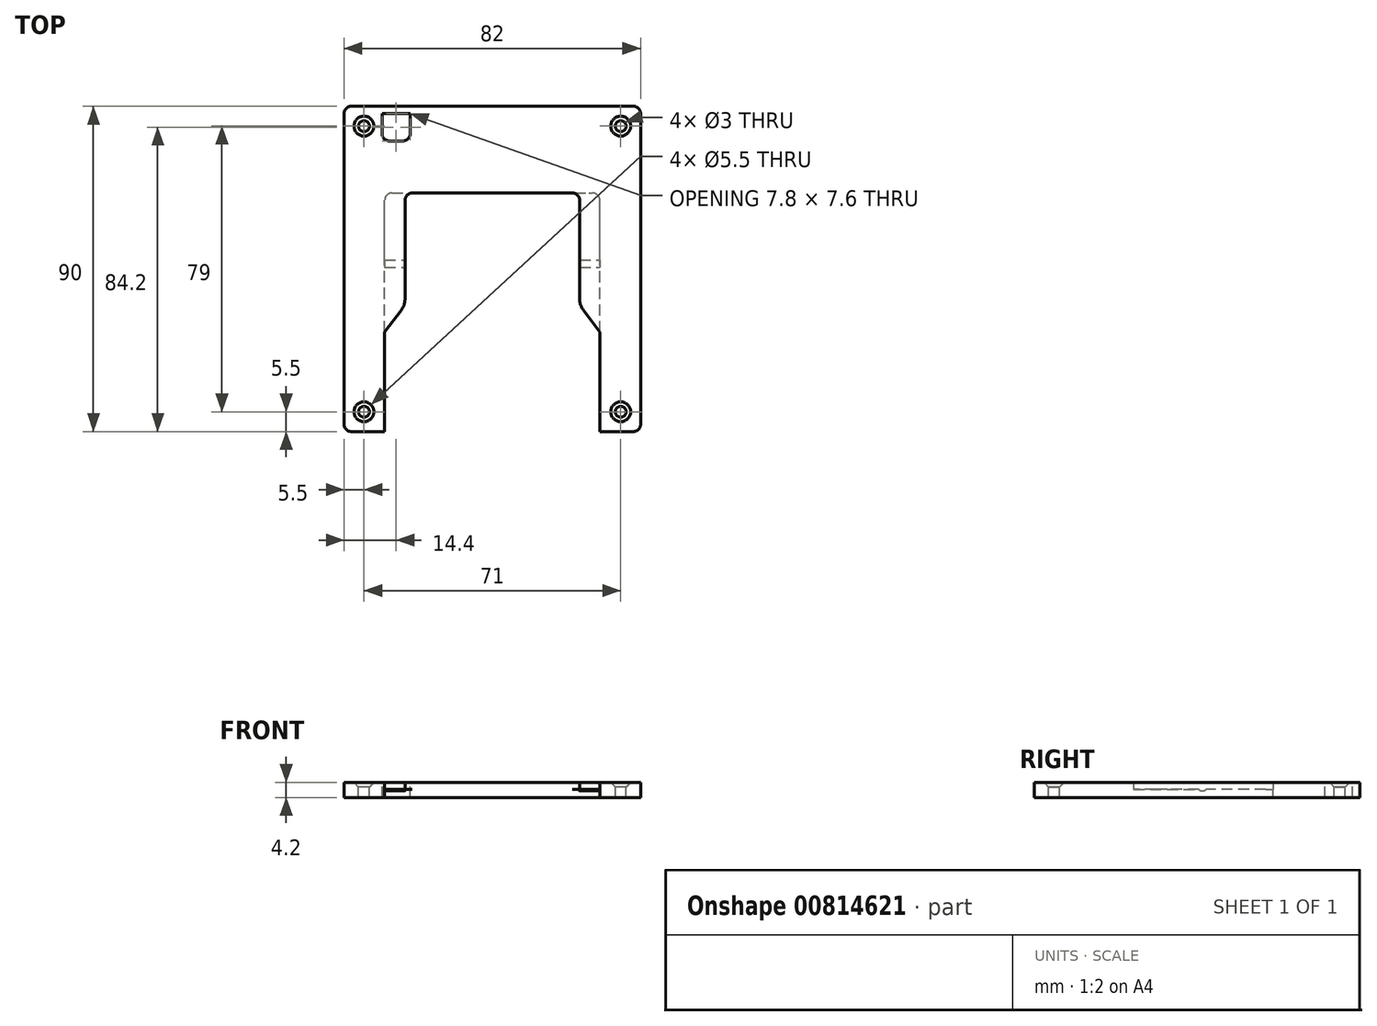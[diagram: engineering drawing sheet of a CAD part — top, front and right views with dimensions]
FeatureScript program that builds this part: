
annotation { "Feature Type Name" : "Feature", "Feature Type Description" : "" }
export const myFeature = defineFeature(function(context is Context, id is Id, definition is map)
    precondition{}
    {
        {
            var Q0;
            Q0=qCreatedBy(makeId("Top.planeOp"),FACE);
            var sketch = newSketch(context, id + "F0", { "sketchPlane" : qUnion([Q0])});
            skLineSegment(sketch, "E0.bottom", {"start": v(2, 0) * mm, "end": v(80, 0) * mm});
            skLineSegment(sketch, "E0.top", {"start": v(2, -90) * mm, "end": v(11.25, -90) * mm});
            skLineSegment(sketch, "E0.left", {"start": v(0, -2) * mm, "end": v(0, -88) * mm});
            skLineSegment(sketch, "E0.right", {"start": v(82, -2) * mm, "end": v(82, -88) * mm});
            skPoint(sketch, "E1.visualSharp", {"position": v(0, 0) * mm});
            skArc(sketch, "E1.filletArc", {"start": v(2, 0) * mm, "mid": v(0.59, -0.59) * mm, "end": v(0, -2) * mm});
            skPoint(sketch, "E2.visualSharp", {"position": v(82, 0) * mm});
            skArc(sketch, "E2.filletArc", {"start": v(82, -2) * mm, "mid": v(81.41, -0.59) * mm, "end": v(80, 0) * mm});
            skPoint(sketch, "E3.visualSharp", {"position": v(82, -90) * mm});
            skArc(sketch, "E3.filletArc", {"start": v(80, -90) * mm, "mid": v(81.41, -89.41) * mm, "end": v(82, -88) * mm});
            skPoint(sketch, "E4.visualSharp", {"position": v(0, -90) * mm});
            skArc(sketch, "E4.filletArc", {"start": v(0, -88) * mm, "mid": v(0.59, -89.41) * mm, "end": v(2, -90) * mm});
            skLineSegment(sketch, "E5.top", {"start": v(18.85, -24) * mm, "end": v(63.15, -24) * mm});
            skLineSegment(sketch, "E5.left", {"start": v(11.25, -90) * mm, "end": v(11.25, -62.5) * mm});
            skLineSegment(sketch, "E5.right", {"start": v(70.75, -90) * mm, "end": v(70.75, -62.5) * mm});
            skLineSegment(sketch, "E6.trimOffspring", {"start": v(70.75, -90) * mm, "end": v(80, -90) * mm});
            skLineSegment(sketch, "E7.right", {"start": v(16.85, -26) * mm, "end": v(16.85, -53.34) * mm});
            skLineSegment(sketch, "E8.right", {"start": v(65.15, -26) * mm, "end": v(65.15, -53.34) * mm});
            skPoint(sketch, "E9.visualSharp", {"position": v(16.85, -24) * mm});
            skArc(sketch, "E9.filletArc", {"start": v(18.85, -24) * mm, "mid": v(17.44, -24.59) * mm, "end": v(16.85, -26) * mm});
            skPoint(sketch, "E10.visualSharp", {"position": v(65.15, -24) * mm});
            skArc(sketch, "E10.filletArc", {"start": v(65.15, -26) * mm, "mid": v(64.56, -24.59) * mm, "end": v(63.15, -24) * mm});
            skPoint(sketch, "E11", {"position": v(16.85, -55) * mm});
            skLineSegment(sketch, "E12", {"start": v(11.25, -62.5) * mm, "end": v(15.86, -56.33) * mm});
            skLineSegment(sketch, "E13", {"start": v(66.14, -56.33) * mm, "end": v(70.75, -62.5) * mm});
            skArc(sketch, "E14.filletArc", {"start": v(15.86, -56.33) * mm, "mid": v(16.6, -54.92) * mm, "end": v(16.85, -53.34) * mm});
            skPoint(sketch, "E15.visualSharp", {"position": v(65.15, -55) * mm});
            skArc(sketch, "E15.filletArc", {"start": v(65.15, -53.34) * mm, "mid": v(65.4, -54.92) * mm, "end": v(66.14, -56.33) * mm});
            skSolve(sketch);
        }
        {
            var Q0;
            Q0=makeQuery(id+"F0.imprint","IMPRINT",FACE,{"disambiguationData":[TD([[makeQuery(id+"F0.imprint","IMPRINT",EDGE,{"derivedFrom":sQuery(id+"F0.wireOp",EDGE,"E0.bottom")}),-1.0]])]});
            extrude(context, id + "F1", {"entities" : qUnion([Q0]), "depth" : 2 * mm, "offsetDistance" : 25 * mm});
        }
        {
            var Q0;
            Q0=makeQuery(id+"F1.opExtrude","CAP_FACE",FACE,{"disambiguationData":[OSD([sQuery(id+"F0.wireOp",EDGE,"E0.bottom"),sQuery(id+"F0.wireOp",EDGE,"E0.top"),sQuery(id+"F0.wireOp",EDGE,"E0.left"),sQuery(id+"F0.wireOp",EDGE,"E0.right"),sQuery(id+"F0.wireOp",EDGE,"E1.filletArc"),sQuery(id+"F0.wireOp",EDGE,"E2.filletArc"),sQuery(id+"F0.wireOp",EDGE,"E3.filletArc"),sQuery(id+"F0.wireOp",EDGE,"E4.filletArc"),sQuery(id+"F0.wireOp",EDGE,"E5.top"),sQuery(id+"F0.wireOp",EDGE,"E5.left"),sQuery(id+"F0.wireOp",EDGE,"E5.right"),sQuery(id+"F0.wireOp",EDGE,"E6.trimOffspring"),sQuery(id+"F0.wireOp",EDGE,"E7.right"),sQuery(id+"F0.wireOp",EDGE,"E8.right"),sQuery(id+"F0.wireOp",EDGE,"E9.filletArc"),sQuery(id+"F0.wireOp",EDGE,"E10.filletArc"),sQuery(id+"F0.wireOp",EDGE,"E12"),sQuery(id+"F0.wireOp",EDGE,"E13"),sQuery(id+"F0.wireOp",EDGE,"E14.filletArc"),sQuery(id+"F0.wireOp",EDGE,"E15.filletArc")])],"isStart":true});
            var sketch = newSketch(context, id + "F2", { "sketchPlane" : qUnion([Q0])});
            skArc(sketch, "E16.0", {"start": v(82, 2) * mm, "mid": v(81.41, 0.59) * mm, "end": v(80, 0) * mm});
            skLineSegment(sketch, "E16.1", {"start": v(2, 0) * mm, "end": v(80, 0) * mm});
            skArc(sketch, "E16.2", {"start": v(2, 0) * mm, "mid": v(0.59, 0.59) * mm, "end": v(0, 2) * mm});
            skLineSegment(sketch, "E16.3", {"start": v(0, 2) * mm, "end": v(0, 88) * mm});
            skArc(sketch, "E16.4", {"start": v(0, 88) * mm, "mid": v(0.59, 89.41) * mm, "end": v(2, 90) * mm});
            skLineSegment(sketch, "E16.5", {"start": v(82, 2) * mm, "end": v(82, 88) * mm});
            skLineSegment(sketch, "E16.6", {"start": v(2, 90) * mm, "end": v(11.25, 90) * mm});
            skLineSegment(sketch, "E16.7", {"start": v(11.25, 90) * mm, "end": v(11.25, 62.5) * mm});
            skLineSegment(sketch, "E16.9", {"start": v(70.75, 90) * mm, "end": v(70.75, 62.5) * mm});
            skLineSegment(sketch, "E16.10", {"start": v(70.75, 90) * mm, "end": v(80, 90) * mm});
            skArc(sketch, "E16.11", {"start": v(80, 90) * mm, "mid": v(81.41, 89.41) * mm, "end": v(82, 88) * mm});
            skLineSegment(sketch, "E16.14", {"start": v(16.85, 24) * mm, "end": v(65.15, 24) * mm});
            skLineSegment(sketch, "E17", {"start": v(70.75, 62.5) * mm, "end": v(70.75, 26) * mm});
            skLineSegment(sketch, "E18", {"start": v(68.75, 24) * mm, "end": v(65.15, 24) * mm});
            skPoint(sketch, "E19.visualSharp", {"position": v(70.75, 24) * mm});
            skArc(sketch, "E19.filletArc", {"start": v(68.75, 24) * mm, "mid": v(70.16, 24.59) * mm, "end": v(70.75, 26) * mm});
            skLineSegment(sketch, "E20", {"start": v(11.25, 62.5) * mm, "end": v(11.25, 26) * mm});
            skLineSegment(sketch, "E21", {"start": v(13.25, 24) * mm, "end": v(16.85, 24) * mm});
            skPoint(sketch, "E22.visualSharp", {"position": v(11.25, 24) * mm});
            skArc(sketch, "E22.filletArc", {"start": v(11.25, 26) * mm, "mid": v(11.84, 24.59) * mm, "end": v(13.25, 24) * mm});
            skSolve(sketch);
        }
        {
            var Q0;
            Q0=qSketchRegion(id+"F2",true);
            extrude(context, id + "F3", {"entities" : qUnion([Q0]), "operationType" : NewBodyOperationType.ADD, "depth" : 2.2 * mm, "offsetDistance" : 25 * mm});
        }
        {
            var Q0;
            Q0=makeQuery(id+"F1.opExtrude","CAP_FACE",FACE,{"disambiguationData":[OSD([sQuery(id+"F0.wireOp",EDGE,"E0.bottom"),sQuery(id+"F0.wireOp",EDGE,"E0.top"),sQuery(id+"F0.wireOp",EDGE,"E0.left"),sQuery(id+"F0.wireOp",EDGE,"E0.right"),sQuery(id+"F0.wireOp",EDGE,"E1.filletArc"),sQuery(id+"F0.wireOp",EDGE,"E2.filletArc"),sQuery(id+"F0.wireOp",EDGE,"E3.filletArc"),sQuery(id+"F0.wireOp",EDGE,"E4.filletArc"),sQuery(id+"F0.wireOp",EDGE,"E5.top"),sQuery(id+"F0.wireOp",EDGE,"E5.left"),sQuery(id+"F0.wireOp",EDGE,"E5.right"),sQuery(id+"F0.wireOp",EDGE,"E6.trimOffspring"),sQuery(id+"F0.wireOp",EDGE,"E7.right"),sQuery(id+"F0.wireOp",EDGE,"E8.right"),sQuery(id+"F0.wireOp",EDGE,"E9.filletArc"),sQuery(id+"F0.wireOp",EDGE,"E10.filletArc"),sQuery(id+"F0.wireOp",EDGE,"E12"),sQuery(id+"F0.wireOp",EDGE,"E13"),sQuery(id+"F0.wireOp",EDGE,"E14.filletArc"),sQuery(id+"F0.wireOp",EDGE,"E15.filletArc")])],"isStart":false});
            var sketch = newSketch(context, id + "F4", { "sketchPlane" : qUnion([Q0])});
            skLineSegment(sketch, "E23.bottom", {"start": v(10.5, -2) * mm, "end": v(18.3, -2) * mm});
            skLineSegment(sketch, "E23.top", {"start": v(12.5, -9.6) * mm, "end": v(16.3, -9.6) * mm});
            skLineSegment(sketch, "E23.left", {"start": v(10.5, -2) * mm, "end": v(10.5, -7.6) * mm});
            skLineSegment(sketch, "E23.right", {"start": v(18.3, -2) * mm, "end": v(18.3, -7.6) * mm});
            skPoint(sketch, "E24.visualSharp", {"position": v(10.5, -9.6) * mm});
            skArc(sketch, "E24.filletArc", {"start": v(10.5, -7.6) * mm, "mid": v(11.09, -9.01) * mm, "end": v(12.5, -9.6) * mm});
            skPoint(sketch, "E25.visualSharp", {"position": v(18.3, -9.6) * mm});
            skArc(sketch, "E25.filletArc", {"start": v(16.3, -9.6) * mm, "mid": v(17.71, -9.01) * mm, "end": v(18.3, -7.6) * mm});
            skSolve(sketch);
        }
        {
            var Q0;
            Q0=qSketchRegion(id+"F4",true);
            extrude(context, id + "F5", {"entities" : qUnion([Q0]), "operationType" : NewBodyOperationType.REMOVE, "oppositeDirection" : true, "depth" : 25 * mm, "offsetDistance" : 25 * mm});
        }
        {
            var Q0;
            Q0=makeQuery(id+"F1.opExtrude","CAP_FACE",FACE,{"disambiguationData":[OSD([sQuery(id+"F0.wireOp",EDGE,"E0.bottom"),sQuery(id+"F0.wireOp",EDGE,"E0.top"),sQuery(id+"F0.wireOp",EDGE,"E0.left"),sQuery(id+"F0.wireOp",EDGE,"E0.right"),sQuery(id+"F0.wireOp",EDGE,"E1.filletArc"),sQuery(id+"F0.wireOp",EDGE,"E2.filletArc"),sQuery(id+"F0.wireOp",EDGE,"E3.filletArc"),sQuery(id+"F0.wireOp",EDGE,"E4.filletArc"),sQuery(id+"F0.wireOp",EDGE,"E5.top"),sQuery(id+"F0.wireOp",EDGE,"E5.left"),sQuery(id+"F0.wireOp",EDGE,"E5.right"),sQuery(id+"F0.wireOp",EDGE,"E6.trimOffspring"),sQuery(id+"F0.wireOp",EDGE,"E7.right"),sQuery(id+"F0.wireOp",EDGE,"E8.right"),sQuery(id+"F0.wireOp",EDGE,"E9.filletArc"),sQuery(id+"F0.wireOp",EDGE,"E10.filletArc"),sQuery(id+"F0.wireOp",EDGE,"E12"),sQuery(id+"F0.wireOp",EDGE,"E13"),sQuery(id+"F0.wireOp",EDGE,"E14.filletArc"),sQuery(id+"F0.wireOp",EDGE,"E15.filletArc")])],"isStart":false});
            var sketch = newSketch(context, id + "F6", { "sketchPlane" : qUnion([Q0])});
            skCircle(sketch, "E26", {"center": v(5.5, -5.5) * mm, "radius": 1.5 * mm});
            skCircle(sketch, "E27", {"center": v(76.5, -5.5) * mm, "radius": 1.5 * mm});
            skCircle(sketch, "E28", {"center": v(5.5, -84.5) * mm, "radius": 1.5 * mm});
            skCircle(sketch, "E29", {"center": v(76.5, -84.5) * mm, "radius": 1.5 * mm});
            skSolve(sketch);
        }
        {
            var Q0;
            Q0=makeQuery(id+"F6.imprint","IMPRINT",FACE,{"disambiguationData":[TD([[makeQuery(id+"F6.imprint","IMPRINT",EDGE,{"derivedFrom":sQuery(id+"F6.wireOp",EDGE,"E28")}),1.0]])]});
            var Q1;
            Q1=makeQuery(id+"F6.imprint","IMPRINT",FACE,{"disambiguationData":[TD([[makeQuery(id+"F6.imprint","IMPRINT",EDGE,{"derivedFrom":sQuery(id+"F6.wireOp",EDGE,"E29")}),1.0]])]});
            var Q2;
            Q2=makeQuery(id+"F6.imprint","IMPRINT",FACE,{"disambiguationData":[TD([[makeQuery(id+"F6.imprint","IMPRINT",EDGE,{"derivedFrom":sQuery(id+"F6.wireOp",EDGE,"E26")}),1.0]])]});
            var Q3;
            Q3=makeQuery(id+"F6.imprint","IMPRINT",FACE,{"disambiguationData":[TD([[makeQuery(id+"F6.imprint","IMPRINT",EDGE,{"derivedFrom":sQuery(id+"F6.wireOp",EDGE,"E27")}),1.0]])]});
            extrude(context, id + "F7", {"entities" : qUnion([Q0, Q1, Q2, Q3]), "operationType" : NewBodyOperationType.REMOVE, "oppositeDirection" : true, "depth" : 4.2 * mm, "offsetDistance" : 25 * mm});
        }
        {
            var Q0;
            Q0=makeQuery(id+"F1.opExtrude","CAP_FACE",FACE,{"disambiguationData":[OSD([sQuery(id+"F0.wireOp",EDGE,"E0.bottom"),sQuery(id+"F0.wireOp",EDGE,"E0.top"),sQuery(id+"F0.wireOp",EDGE,"E0.left"),sQuery(id+"F0.wireOp",EDGE,"E0.right"),sQuery(id+"F0.wireOp",EDGE,"E1.filletArc"),sQuery(id+"F0.wireOp",EDGE,"E2.filletArc"),sQuery(id+"F0.wireOp",EDGE,"E3.filletArc"),sQuery(id+"F0.wireOp",EDGE,"E4.filletArc"),sQuery(id+"F0.wireOp",EDGE,"E5.top"),sQuery(id+"F0.wireOp",EDGE,"E5.left"),sQuery(id+"F0.wireOp",EDGE,"E5.right"),sQuery(id+"F0.wireOp",EDGE,"E6.trimOffspring"),sQuery(id+"F0.wireOp",EDGE,"E7.right"),sQuery(id+"F0.wireOp",EDGE,"E8.right"),sQuery(id+"F0.wireOp",EDGE,"E9.filletArc"),sQuery(id+"F0.wireOp",EDGE,"E10.filletArc"),sQuery(id+"F0.wireOp",EDGE,"E12"),sQuery(id+"F0.wireOp",EDGE,"E13"),sQuery(id+"F0.wireOp",EDGE,"E14.filletArc"),sQuery(id+"F0.wireOp",EDGE,"E15.filletArc")])],"isStart":false});
            var sketch = newSketch(context, id + "F8", { "sketchPlane" : qUnion([Q0])});
            skCircle(sketch, "E30", {"center": v(5.5, -5.5) * mm, "radius": 2.75 * mm});
            skCircle(sketch, "E31", {"center": v(76.5, -5.5) * mm, "radius": 2.75 * mm});
            skCircle(sketch, "E32", {"center": v(76.5, -84.5) * mm, "radius": 2.75 * mm});
            skCircle(sketch, "E33", {"center": v(5.5, -84.5) * mm, "radius": 2.75 * mm});
            skSolve(sketch);
        }
        {
            var Q0;
            Q0=qSketchRegion(id+"F8",true);
            extrude(context, id + "F9", {"entities" : qUnion([Q0]), "operationType" : NewBodyOperationType.REMOVE, "oppositeDirection" : true, "depth" : 1.6 * mm, "offsetDistance" : 25 * mm});
        }
        {
            var Q0;
            Q0=makeQuery(id+"F9.boolean.opBoolean","COPY",EDGE,{"derivedFrom":makeQuery(id+"F9.opExtrude","CAP_EDGE",EDGE,{"disambiguationData":[OSD([sQuery(id+"F8.wireOp",EDGE,"E33")])],"isStart":false})});
            var Q1;
            Q1=makeQuery(id+"F9.boolean.opBoolean","COPY",EDGE,{"derivedFrom":makeQuery(id+"F9.opExtrude","CAP_EDGE",EDGE,{"disambiguationData":[OSD([sQuery(id+"F8.wireOp",EDGE,"E32")])],"isStart":false})});
            var Q2;
            Q2=makeQuery(id+"F9.boolean.opBoolean","COPY",EDGE,{"derivedFrom":makeQuery(id+"F9.opExtrude","CAP_EDGE",EDGE,{"disambiguationData":[OSD([sQuery(id+"F8.wireOp",EDGE,"E30")])],"isStart":false})});
            var Q3;
            Q3=makeQuery(id+"F9.boolean.opBoolean","COPY",EDGE,{"derivedFrom":makeQuery(id+"F9.opExtrude","CAP_EDGE",EDGE,{"disambiguationData":[OSD([sQuery(id+"F8.wireOp",EDGE,"E31")])],"isStart":false})});
            chamfer(context, id + "F10", {"entities" : qUnion([Q0, Q1, Q2, Q3]), "width" : 1.5 * mm, "tangentPropagation" : true});
        }
        {
            var Q0;
            {var subQ0=sQuery(id+"F0.wireOp",EDGE,"E7.right");var subQ1=sQuery(id+"F0.wireOp",EDGE,"E9.filletArc");var subQ2=sQuery(id+"F0.wireOp",EDGE,"E5.left");var subQ3=sQuery(id+"F0.wireOp",EDGE,"E5.top");var subQ4=sQuery(id+"F0.wireOp",EDGE,"E12");var subQ5=sQuery(id+"F0.wireOp",EDGE,"E14.filletArc");Q0=makeQuery(id+"F3.boolean.opBoolean","SPLIT",FACE,{"disambiguationData":[TD([makeQuery(id+"F1.opExtrude","SWEPT_FACE",FACE,{"disambiguationData":[OSD([subQ2])]})])],"derivedFrom":makeQuery(id+"F1.opExtrude","CAP_FACE",FACE,{"disambiguationData":[OSD([sQuery(id+"F0.wireOp",EDGE,"E0.bottom"),sQuery(id+"F0.wireOp",EDGE,"E0.top"),sQuery(id+"F0.wireOp",EDGE,"E0.left"),sQuery(id+"F0.wireOp",EDGE,"E0.right"),sQuery(id+"F0.wireOp",EDGE,"E1.filletArc"),sQuery(id+"F0.wireOp",EDGE,"E2.filletArc"),sQuery(id+"F0.wireOp",EDGE,"E3.filletArc"),sQuery(id+"F0.wireOp",EDGE,"E4.filletArc"),subQ3,subQ2,sQuery(id+"F0.wireOp",EDGE,"E5.right"),sQuery(id+"F0.wireOp",EDGE,"E6.trimOffspring"),subQ0,sQuery(id+"F0.wireOp",EDGE,"E8.right"),subQ1,sQuery(id+"F0.wireOp",EDGE,"E10.filletArc"),subQ4,sQuery(id+"F0.wireOp",EDGE,"E13"),subQ5,sQuery(id+"F0.wireOp",EDGE,"E15.filletArc")])],"isStart":true})});}
            var sketch = newSketch(context, id + "F11", { "sketchPlane" : qUnion([Q0])});
            skLineSegment(sketch, "E34.bottom", {"start": v(11.25, 44.5) * mm, "end": v(16.85, 44.5) * mm});
            skLineSegment(sketch, "E34.top", {"start": v(11.25, 42.5) * mm, "end": v(16.85, 42.5) * mm});
            skLineSegment(sketch, "E34.left", {"start": v(11.25, 44.5) * mm, "end": v(11.25, 42.5) * mm});
            skLineSegment(sketch, "E34.right", {"start": v(16.85, 44.5) * mm, "end": v(16.85, 42.5) * mm});
            skLineSegment(sketch, "E35.bottom", {"start": v(65.15, 42.5) * mm, "end": v(70.75, 42.5) * mm});
            skLineSegment(sketch, "E35.top", {"start": v(65.15, 44.5) * mm, "end": v(70.75, 44.5) * mm});
            skLineSegment(sketch, "E35.left", {"start": v(65.15, 42.5) * mm, "end": v(65.15, 44.5) * mm});
            skLineSegment(sketch, "E35.right", {"start": v(70.75, 42.5) * mm, "end": v(70.75, 44.5) * mm});
            skSolve(sketch);
        }
        {
            var Q0;
            Q0=qSketchRegion(id+"F11",true);
            extrude(context, id + "F12", {"entities" : qUnion([Q0]), "operationType" : NewBodyOperationType.ADD, "depth" : 0.4 * mm, "offsetDistance" : 25 * mm});
        }
        {
            var Q0;
            Q0=makeQuery(id+"F12.opExtrude","CAP_EDGE",EDGE,{"disambiguationData":[OSD([sQuery(id+"F11.wireOp",EDGE,"E34.top")])],"isStart":false});
            var Q1;
            Q1=makeQuery(id+"F12.opExtrude","CAP_EDGE",EDGE,{"disambiguationData":[OSD([sQuery(id+"F11.wireOp",EDGE,"E34.bottom")])],"isStart":false});
            var Q2;
            Q2=makeQuery(id+"F12.opExtrude","CAP_EDGE",EDGE,{"disambiguationData":[OSD([sQuery(id+"F11.wireOp",EDGE,"E35.bottom")])],"isStart":false});
            var Q3;
            Q3=makeQuery(id+"F12.opExtrude","CAP_EDGE",EDGE,{"disambiguationData":[OSD([sQuery(id+"F11.wireOp",EDGE,"E35.top")])],"isStart":false});
            fillet(context, id + "F13", {"entities" : qUnion([Q0, Q1, Q2, Q3]), "radius" : 1.4 * mm, "tangentPropagation" : true, "allowEdgeOverflow" : false});
        }
    });
